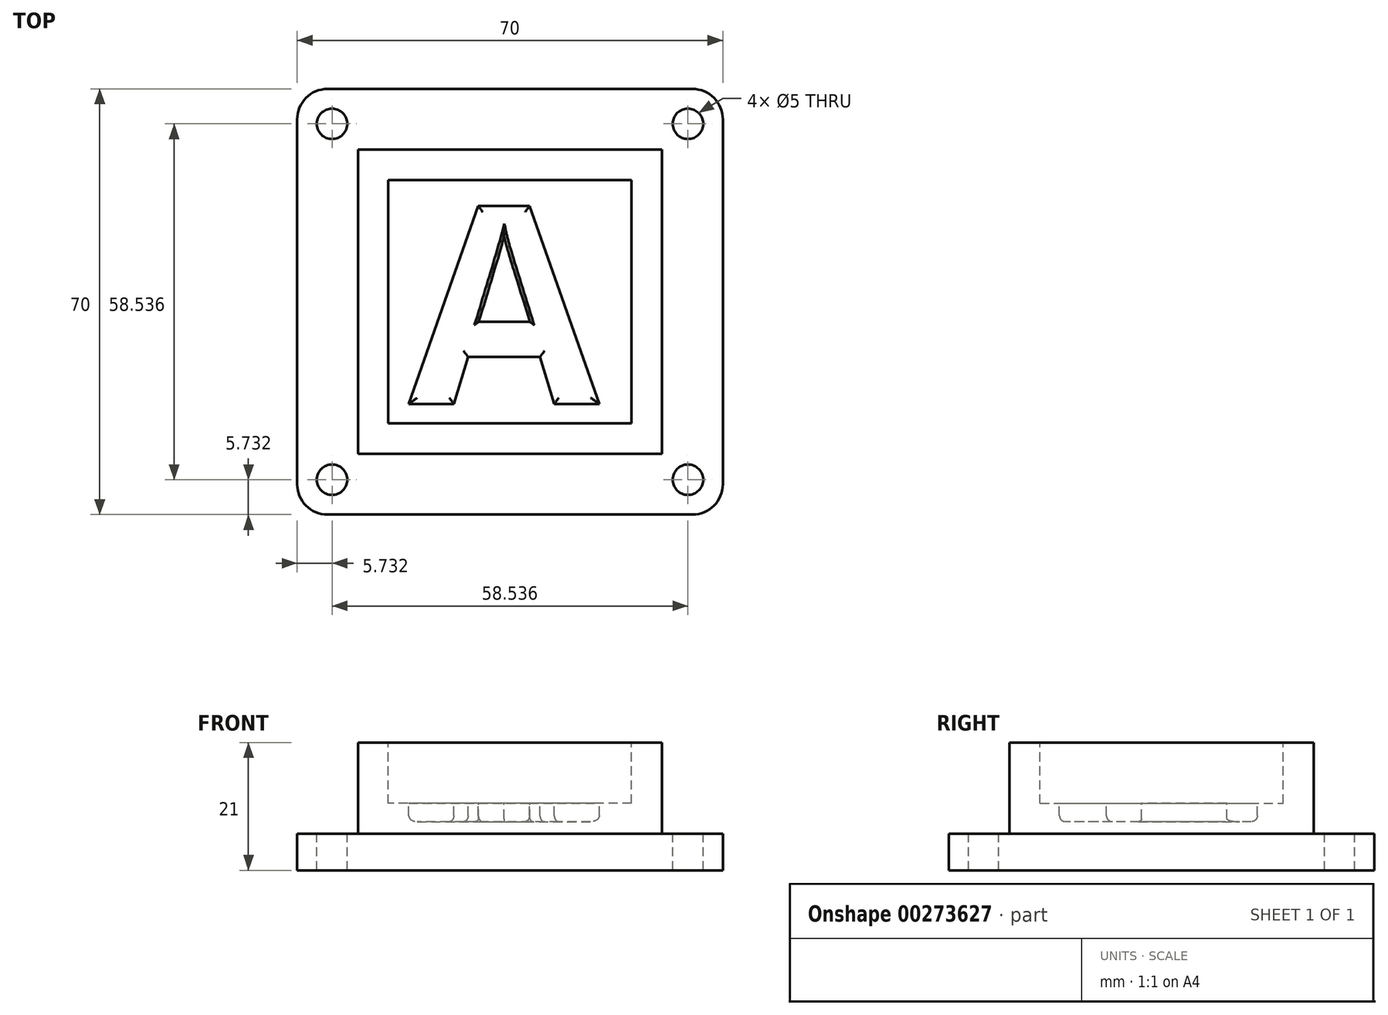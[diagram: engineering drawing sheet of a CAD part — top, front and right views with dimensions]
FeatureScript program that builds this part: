
annotation { "Feature Type Name" : "Feature", "Feature Type Description" : "" }
export const myFeature = defineFeature(function(context is Context, id is Id, definition is map)
    precondition{}
    {
        {
            var Q0;
            Q0=qCreatedBy(makeId("Top.planeOp"),FACE);
            var sketch = newSketch(context, id + "F0", { "sketchPlane" : qUnion([Q0])});
            skLineSegment(sketch, "E0.bottom", {"start": v(35, -35) * mm, "end": v(-35, -35) * mm});
            skLineSegment(sketch, "E0.top", {"start": v(35, 35) * mm, "end": v(-35, 35) * mm});
            skLineSegment(sketch, "E0.left", {"start": v(35, -35) * mm, "end": v(35, 35) * mm});
            skLineSegment(sketch, "E0.right", {"start": v(-35, -35) * mm, "end": v(-35, 35) * mm});
            skPoint(sketch, "E0.middle", {"position": v(0, 0) * mm});
            skSolve(sketch);
        }
        {
            var Q0;
            Q0=makeQuery(id+"F0.imprint","IMPRINT",FACE,{"disambiguationData":[TD([[makeQuery(id+"F0.imprint","IMPRINT",EDGE,{"derivedFrom":sQuery(id+"F0.wireOp",EDGE,"E0.bottom")}),-1.0]])]});
            extrude(context, id + "F1", {"entities" : qUnion([Q0]), "depth" : 6 * mm});
        }
        {
            var Q0;
            Q0=makeQuery(id+"F1.opExtrude","CAP_FACE",FACE,{"disambiguationData":[OSD([sQuery(id+"F0.wireOp",EDGE,"E0.bottom"),sQuery(id+"F0.wireOp",EDGE,"E0.top"),sQuery(id+"F0.wireOp",EDGE,"E0.left"),sQuery(id+"F0.wireOp",EDGE,"E0.right")])],"isStart":false});
            var sketch = newSketch(context, id + "F2", { "sketchPlane" : qUnion([Q0])});
            skLineSegment(sketch, "E1.bottom", {"start": v(25, -25) * mm, "end": v(-25, -25) * mm});
            skLineSegment(sketch, "E1.top", {"start": v(25, 25) * mm, "end": v(-25, 25) * mm});
            skLineSegment(sketch, "E1.left", {"start": v(25, -25) * mm, "end": v(25, 25) * mm});
            skLineSegment(sketch, "E1.right", {"start": v(-25, -25) * mm, "end": v(-25, 25) * mm});
            skPoint(sketch, "E1.middle", {"position": v(0, 0) * mm});
            skSolve(sketch);
        }
        {
            var Q0;
            Q0=makeQuery(id+"F2.imprint","IMPRINT",FACE,{"disambiguationData":[TD([[makeQuery(id+"F2.imprint","IMPRINT",EDGE,{"derivedFrom":sQuery(id+"F2.wireOp",EDGE,"E1.bottom")}),-1.0]])]});
            extrude(context, id + "F3", {"entities" : qUnion([Q0]), "operationType" : NewBodyOperationType.ADD, "depth" : 15 * mm});
        }
        {
            var Q0;
            Q0=makeQuery(id+"F1.opExtrude","SWEPT_EDGE",EDGE,{"disambiguationData":[OSD([sQuery(id+"F0.wireOp",EDGE,"E0.top"),sQuery(id+"F0.wireOp",EDGE,"E0.right")])]});
            var Q1;
            Q1=makeQuery(id+"F1.opExtrude","SWEPT_EDGE",EDGE,{"disambiguationData":[OSD([sQuery(id+"F0.wireOp",EDGE,"E0.top"),sQuery(id+"F0.wireOp",EDGE,"E0.left")])]});
            var Q2;
            Q2=makeQuery(id+"F1.opExtrude","SWEPT_EDGE",EDGE,{"disambiguationData":[OSD([sQuery(id+"F0.wireOp",EDGE,"E0.bottom"),sQuery(id+"F0.wireOp",EDGE,"E0.left")])]});
            var Q3;
            Q3=makeQuery(id+"F1.opExtrude","SWEPT_EDGE",EDGE,{"disambiguationData":[OSD([sQuery(id+"F0.wireOp",EDGE,"E0.bottom"),sQuery(id+"F0.wireOp",EDGE,"E0.right")])]});
            fillet(context, id + "F4", {"entities" : qUnion([Q0, Q1, Q2, Q3]), "radius" : 5 * mm, "tangentPropagation" : true, "allowEdgeOverflow" : false});
        }
        {
            var Q0;
            Q0=makeQuery(id+"F1.opExtrude","CAP_FACE",FACE,{"disambiguationData":[OSD([sQuery(id+"F0.wireOp",EDGE,"E0.bottom"),sQuery(id+"F0.wireOp",EDGE,"E0.top"),sQuery(id+"F0.wireOp",EDGE,"E0.left"),sQuery(id+"F0.wireOp",EDGE,"E0.right")])],"isStart":false});
            var sketch = newSketch(context, id + "F5", { "sketchPlane" : qUnion([Q0])});
            skLineSegment(sketch, "E2.0", {"start": v(-35, -30) * mm, "end": v(-35, 30) * mm, "construction": true});
            skPoint(sketch, "E3.0", {"position": v(-33.54, 33.54) * mm});
            skArc(sketch, "E4.0", {"start": v(-30, 35) * mm, "mid": v(-33.54, 33.54) * mm, "end": v(-35, 30) * mm});
            skLineSegment(sketch, "E5.0", {"start": v(30, 35) * mm, "end": v(-30, 35) * mm, "construction": true});
            skLineSegment(sketch, "E6.0", {"start": v(35, -30) * mm, "end": v(35, 30) * mm, "construction": true});
            skArc(sketch, "E7.0", {"start": v(30, -35) * mm, "mid": v(33.54, -33.54) * mm, "end": v(35, -30) * mm, "construction": true});
            skLineSegment(sketch, "E8.0", {"start": v(30, -35) * mm, "end": v(-30, -35) * mm, "construction": true});
            skArc(sketch, "E9.0", {"start": v(-35, -30) * mm, "mid": v(-33.54, -33.54) * mm, "end": v(-30, -35) * mm, "construction": true});
            skPoint(sketch, "E10.0", {"position": v(33.54, 33.54) * mm});
            skPoint(sketch, "E11", {"position": v(-33.54, -33.54) * mm});
            skPoint(sketch, "E12", {"position": v(33.54, -33.54) * mm});
            skLineSegment(sketch, "E13", {"start": v(-33.54, 33.54) * mm, "end": v(-25, 25) * mm, "construction": true});
            skLineSegment(sketch, "E14", {"start": v(25, 25) * mm, "end": v(33.54, 33.54) * mm, "construction": true});
            skLineSegment(sketch, "E15", {"start": v(25, -25) * mm, "end": v(33.54, -33.54) * mm, "construction": true});
            skLineSegment(sketch, "E16", {"start": v(-25, -25) * mm, "end": v(-33.54, -33.54) * mm, "construction": true});
            skPoint(sketch, "E17", {"position": v(-29.27, 29.27) * mm});
            skPoint(sketch, "E18", {"position": v(29.27, 29.27) * mm});
            skPoint(sketch, "E19", {"position": v(29.27, -29.27) * mm});
            skPoint(sketch, "E20", {"position": v(-29.27, -29.27) * mm});
            skCircle(sketch, "E21", {"center": v(-29.27, 29.27) * mm, "radius": 2.5 * mm});
            skCircle(sketch, "E22", {"center": v(29.27, 29.27) * mm, "radius": 2.5 * mm});
            skCircle(sketch, "E23", {"center": v(29.27, -29.27) * mm, "radius": 2.5 * mm});
            skCircle(sketch, "E24", {"center": v(-29.27, -29.27) * mm, "radius": 2.5 * mm});
            skSolve(sketch);
        }
        {
            var Q0;
            Q0=makeQuery(id+"F5.imprint","IMPRINT",FACE,{"disambiguationData":[TD([[makeQuery(id+"F5.imprint","IMPRINT",EDGE,{"derivedFrom":sQuery(id+"F5.wireOp",EDGE,"E21")}),1.0]])]});
            var Q1;
            Q1=makeQuery(id+"F5.imprint","IMPRINT",FACE,{"disambiguationData":[TD([[makeQuery(id+"F5.imprint","IMPRINT",EDGE,{"derivedFrom":sQuery(id+"F5.wireOp",EDGE,"E22")}),1.0]])]});
            var Q2;
            Q2=makeQuery(id+"F5.imprint","IMPRINT",FACE,{"disambiguationData":[TD([[makeQuery(id+"F5.imprint","IMPRINT",EDGE,{"derivedFrom":sQuery(id+"F5.wireOp",EDGE,"E23")}),1.0]])]});
            var Q3;
            Q3=makeQuery(id+"F5.imprint","IMPRINT",FACE,{"disambiguationData":[TD([[makeQuery(id+"F5.imprint","IMPRINT",EDGE,{"derivedFrom":sQuery(id+"F5.wireOp",EDGE,"E24")}),1.0]])]});
            extrude(context, id + "F6", {"entities" : qUnion([Q0, Q1, Q2, Q3]), "operationType" : NewBodyOperationType.REMOVE, "oppositeDirection" : true, "depth" : 25 * mm});
        }
        {
            var Q0;
            Q0=makeQuery(id+"F3.opExtrude","CAP_FACE",FACE,{"disambiguationData":[OSD([sQuery(id+"F2.wireOp",EDGE,"E1.bottom"),sQuery(id+"F2.wireOp",EDGE,"E1.top"),sQuery(id+"F2.wireOp",EDGE,"E1.left"),sQuery(id+"F2.wireOp",EDGE,"E1.right")])],"isStart":false});
            var sketch = newSketch(context, id + "F7", { "sketchPlane" : qUnion([Q0])});
            skSolve(sketch);
        }
        {
            var Q0;
            Q0=makeQuery(id+"F7.imprint","IMPRINT",FACE,{"disambiguationData":[TD([[makeQuery(id+"F7.imprint","IMPRINT",EDGE,{"derivedFrom":makeQuery(id+"F3.opExtrude","CAP_EDGE",EDGE,{"disambiguationData":[OSD([sQuery(id+"F2.wireOp",EDGE,"E1.bottom")])],"isStart":false})}),-1.0]])]});
            var sketch = newSketch(context, id + "F8", { "sketchPlane" : qUnion([Q0])});
            skLineSegment(sketch, "E25.bottom", {"start": v(20, -20) * mm, "end": v(-20, -20) * mm});
            skLineSegment(sketch, "E25.top", {"start": v(20, 20) * mm, "end": v(-20, 20) * mm});
            skLineSegment(sketch, "E25.left", {"start": v(20, -20) * mm, "end": v(20, 20) * mm});
            skLineSegment(sketch, "E25.right", {"start": v(-20, -20) * mm, "end": v(-20, 20) * mm});
            skPoint(sketch, "E25.middle", {"position": v(0, 0) * mm});
            skSolve(sketch);
        }
        {
            var Q0;
            Q0=makeQuery(id+"F7.imprint","IMPRINT",FACE,{"disambiguationData":[TD([[makeQuery(id+"F7.imprint","IMPRINT",EDGE,{"derivedFrom":makeQuery(id+"F3.opExtrude","CAP_EDGE",EDGE,{"disambiguationData":[OSD([sQuery(id+"F2.wireOp",EDGE,"E1.bottom")])],"isStart":false})}),-1.0]])]});
            var sketch = newSketch(context, id + "F9", { "sketchPlane" : qUnion([Q0])});
            skText(sketch, "E26", { "text": "A", "fontName": "OpenSans-Bold.ttf"});
            const initialGuessF9  = {"E26": [-0.01665, -0.0168, 1, 0, 0.0327]};
            skSetInitialGuess(sketch, initialGuessF9);
            skSolve(sketch);
        }
        {
            var Q0;
            Q0 = qSketchRegion(id + "F8", true);
            var Q1;
            Q1 = qSketchRegion(id + "F9", true);
            extrude(context, id + "F10", {"entities" : qUnion([Q0, Q1]), "operationType" : NewBodyOperationType.REMOVE, "oppositeDirection" : true, "depth" : 10 * mm});
        }
        {
            var Q0;
            Q0 = qSketchRegion(id + "F9", true);
            extrude(context, id + "F11", {"entities" : qUnion([Q0]), "operationType" : NewBodyOperationType.REMOVE, "oppositeDirection" : true, "depth" : 13 * mm});
        }
        {
            var Q0;
            Q0=makeQuery(id+"F11.boolean.opBoolean","COPY",EDGE,{"derivedFrom":makeQuery(id+"F11.opExtrude","CAP_EDGE",EDGE,{"disambiguationData":[OSD([sQuery(id+"F9.wireOp",EDGE,"E26.sketch_text.stroke-4")])],"isStart":false})});
            var Q1;
            Q1=makeQuery(id+"F11.boolean.opBoolean","COPY",EDGE,{"derivedFrom":makeQuery(id+"F11.opExtrude","CAP_EDGE",EDGE,{"disambiguationData":[OSD([sQuery(id+"F9.wireOp",EDGE,"E26.sketch_text.stroke-5")])],"isStart":false})});
            var Q2;
            Q2=makeQuery(id+"F11.boolean.opBoolean","COPY",EDGE,{"derivedFrom":makeQuery(id+"F11.opExtrude","CAP_EDGE",EDGE,{"disambiguationData":[OSD([sQuery(id+"F9.wireOp",EDGE,"E26.sketch_text.stroke-6")])],"isStart":false})});
            var Q3;
            Q3=makeQuery(id+"F11.boolean.opBoolean","COPY",EDGE,{"derivedFrom":makeQuery(id+"F11.opExtrude","CAP_EDGE",EDGE,{"disambiguationData":[OSD([sQuery(id+"F9.wireOp",EDGE,"E26.sketch_text.stroke-0")])],"isStart":false})});
            var Q4;
            Q4=makeQuery(id+"F11.boolean.opBoolean","COPY",EDGE,{"derivedFrom":makeQuery(id+"F11.opExtrude","CAP_EDGE",EDGE,{"disambiguationData":[OSD([sQuery(id+"F9.wireOp",EDGE,"E26.sketch_text.stroke-1")])],"isStart":false})});
            var Q5;
            Q5=makeQuery(id+"F11.boolean.opBoolean","COPY",EDGE,{"derivedFrom":makeQuery(id+"F11.opExtrude","CAP_EDGE",EDGE,{"disambiguationData":[OSD([sQuery(id+"F9.wireOp",EDGE,"E26.sketch_text.stroke-2")])],"isStart":false})});
            var Q6;
            Q6=makeQuery(id+"F11.boolean.opBoolean","COPY",EDGE,{"derivedFrom":makeQuery(id+"F11.opExtrude","CAP_EDGE",EDGE,{"disambiguationData":[OSD([sQuery(id+"F9.wireOp",EDGE,"E26.sketch_text.stroke-7")])],"isStart":false})});
            var Q7;
            Q7=makeQuery(id+"F11.boolean.opBoolean","COPY",EDGE,{"derivedFrom":makeQuery(id+"F11.opExtrude","CAP_EDGE",EDGE,{"disambiguationData":[OSD([sQuery(id+"F9.wireOp",EDGE,"E26.sketch_text.stroke-3")])],"isStart":false})});
            fillet(context, id + "F12", {"entities" : qUnion([Q0, Q1, Q2, Q3, Q4, Q5, Q6, Q7]), "radius" : 1 * mm, "tangentPropagation" : true, "allowEdgeOverflow" : false});
        }
        {
            var Q0;
            Q0=makeQuery(id+"F11.boolean.opBoolean","COPY",EDGE,{"derivedFrom":makeQuery(id+"F11.opExtrude","CAP_EDGE",EDGE,{"disambiguationData":[OSD([sQuery(id+"F9.wireOp",EDGE,"E26.sketch_text.stroke-8")])],"isStart":false})});
            var Q1;
            Q1=makeQuery(id+"F11.boolean.opBoolean","COPY",EDGE,{"derivedFrom":makeQuery(id+"F11.opExtrude","CAP_EDGE",EDGE,{"disambiguationData":[OSD([sQuery(id+"F9.wireOp",EDGE,"E26.sketch_text.stroke-9")])],"isStart":false})});
            var Q2;
            Q2=makeQuery(id+"F11.boolean.opBoolean","COPY",EDGE,{"derivedFrom":makeQuery(id+"F11.opExtrude","CAP_EDGE",EDGE,{"disambiguationData":[OSD([sQuery(id+"F9.wireOp",EDGE,"E26.sketch_text.stroke-11")])],"isStart":false})});
            var Q3;
            Q3=makeQuery(id+"F11.boolean.opBoolean","COPY",EDGE,{"derivedFrom":makeQuery(id+"F11.opExtrude","CAP_EDGE",EDGE,{"disambiguationData":[OSD([sQuery(id+"F9.wireOp",EDGE,"E26.sketch_text.stroke-10")])],"isStart":false})});
            fillet(context, id + "F13", {"entities" : qUnion([Q0, Q1, Q2, Q3]), "radius" : 0.5 * mm, "tangentPropagation" : true, "allowEdgeOverflow" : false});
        }
    });
